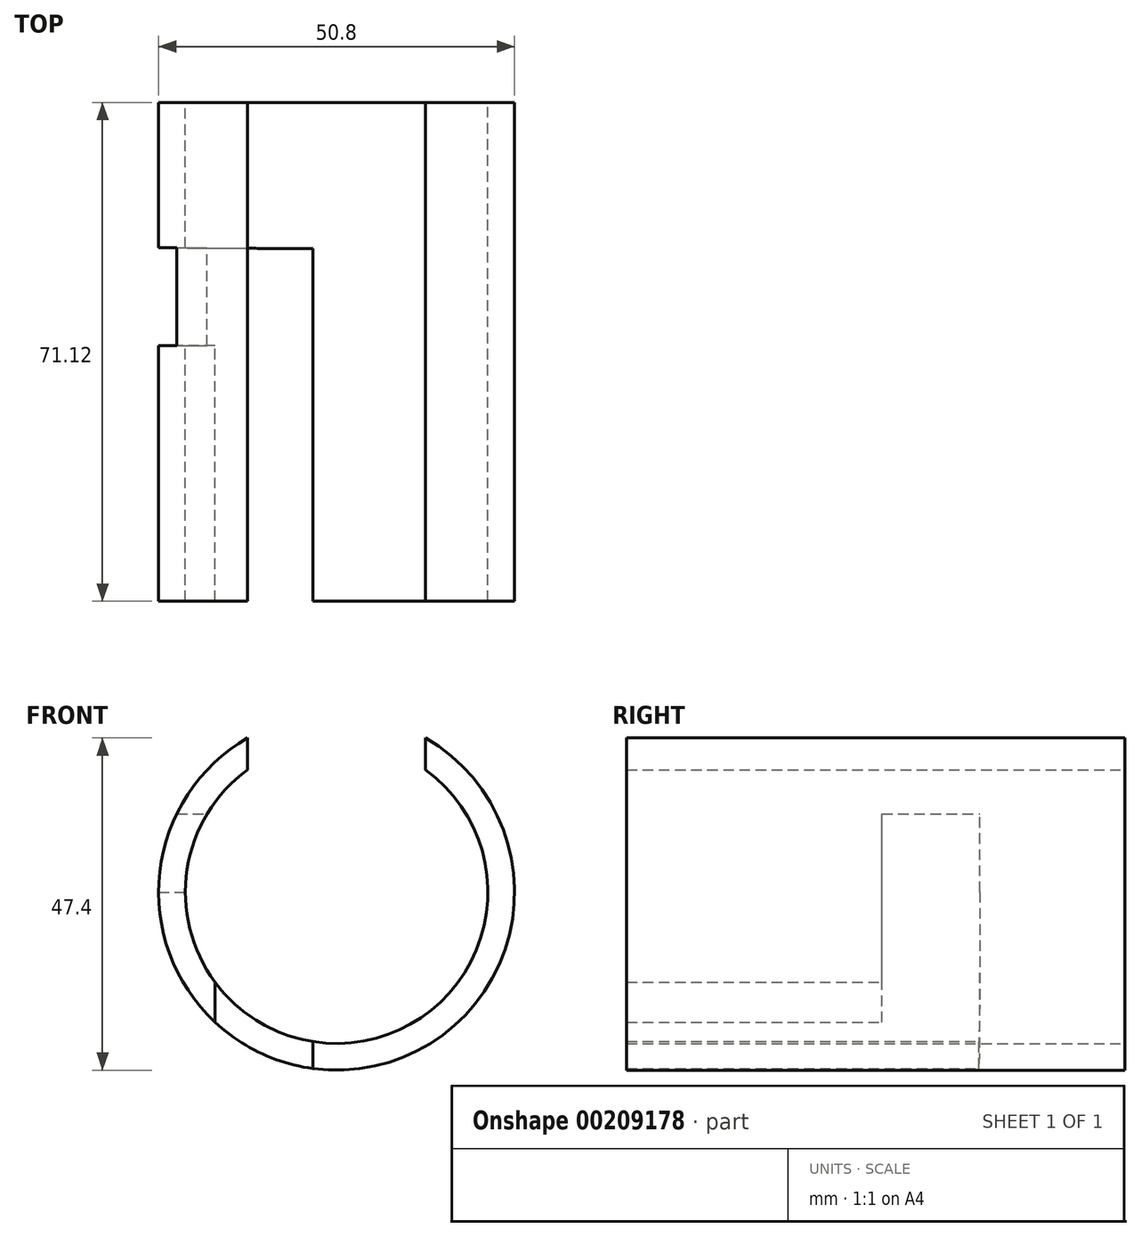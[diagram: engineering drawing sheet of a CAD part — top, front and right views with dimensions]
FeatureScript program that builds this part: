
annotation { "Feature Type Name" : "Feature", "Feature Type Description" : "" }
export const myFeature = defineFeature(function(context is Context, id is Id, definition is map)
    precondition{}
    {
        {
            var Q0;
            Q0=qCreatedBy(makeId("Front.planeOp"),FACE);
            var sketch = newSketch(context, id + "F0", { "sketchPlane" : qUnion([Q0])});
            skCircle(sketch, "E0", {"center": v(0, 0) * mm, "radius": 25.4 * mm});
            skCircle(sketch, "E1.0", {"center": v(0, 0) * mm, "radius": 21.59 * mm});
            skSolve(sketch);
        }
        {
            var Q0;
            Q0=makeQuery(id+"F0.imprint","IMPRINT",FACE,{"disambiguationData":[TD([[makeQuery(id+"F0.imprint","IMPRINT",EDGE,{"derivedFrom":sQuery(id+"F0.wireOp",EDGE,"E0")}),1.0]])]});
            extrude(context, id + "F1", {"entities" : qUnion([Q0]), "depth" : 71.12 * mm});
        }
        {
            var Q0;
            Q0=qCreatedBy(makeId("Top.planeOp"),FACE);
            var sketch = newSketch(context, id + "F2", { "sketchPlane" : qUnion([Q0])});
            skPoint(sketch, "E2", {"position": v(-17.35, -71.12) * mm});
            skPoint(sketch, "E3", {"position": v(-3.38, -71.12) * mm});
            skLineSegment(sketch, "E4", {"start": v(-17.35, -71.12) * mm, "end": v(-17.35, -34.67) * mm});
            skLineSegment(sketch, "E5", {"start": v(-3.38, -71.12) * mm, "end": v(-3.38, -34.67) * mm});
            skLineSegment(sketch, "E6", {"start": v(-3.38, -20.84) * mm, "end": v(-3.38, -34.67) * mm});
            skLineSegment(sketch, "E7", {"start": v(-17.35, -71.12) * mm, "end": v(-3.38, -71.12) * mm});
            skLineSegment(sketch, "E8", {"start": v(-17.35, -34.67) * mm, "end": v(-25.6, -34.67) * mm});
            skLineSegment(sketch, "E9", {"start": v(-25.6, -34.67) * mm, "end": v(-25.59, -20.7) * mm});
            skLineSegment(sketch, "E10", {"start": v(-25.59, -20.7) * mm, "end": v(-3.38, -20.84) * mm});
            skSolve(sketch);
        }
        {
            var Q0;
            Q0 = qSketchRegion(id + "F2", true);
            extrude(context, id + "F3", {"entities" : qUnion([Q0]), "operationType" : NewBodyOperationType.REMOVE, "oppositeDirection" : true, "depth" : 25.4 * mm});
        }
        {
            var Q0;
            Q0=qCreatedBy(makeId("Right.planeOp"),FACE);
            var sketch = newSketch(context, id + "F4", { "sketchPlane" : qUnion([Q0])});
            skPoint(sketch, "E11", {"position": v(-20.7, 0) * mm});
            skPoint(sketch, "E12", {"position": v(-34.67, 0) * mm});
            skLineSegment(sketch, "E13", {"start": v(-20.7, 0) * mm, "end": v(-20.7, 11.16) * mm});
            skLineSegment(sketch, "E14", {"start": v(-20.7, 11.16) * mm, "end": v(-34.67, 11.16) * mm});
            skLineSegment(sketch, "E15", {"start": v(-34.67, 11.16) * mm, "end": v(-34.67, 0) * mm});
            skLineSegment(sketch, "E16", {"start": v(-20.7, 0) * mm, "end": v(-34.67, 0) * mm});
            skSolve(sketch);
        }
        {
            var Q0;
            Q0 = qSketchRegion(id + "F4", true);
            extrude(context, id + "F5", {"entities" : qUnion([Q0]), "operationType" : NewBodyOperationType.REMOVE, "oppositeDirection" : true, "depth" : 25.4 * mm});
        }
        {
            var Q0;
            Q0=qCreatedBy(makeId("Top.planeOp"),FACE);
            var sketch = newSketch(context, id + "F6", { "sketchPlane" : qUnion([Q0])});
            skPoint(sketch, "E17", {"position": v(0, 0) * mm});
            skPoint(sketch, "E18", {"position": v(-12.7, 0) * mm});
            skPoint(sketch, "E19", {"position": v(12.7, 0) * mm});
            skLineSegment(sketch, "E20", {"start": v(-12.7, 0) * mm, "end": v(-12.7, -71.12) * mm});
            skLineSegment(sketch, "E21", {"start": v(12.7, -71.12) * mm, "end": v(12.7, 0) * mm});
            skLineSegment(sketch, "E22", {"start": v(-12.7, -71.12) * mm, "end": v(12.7, -71.12) * mm});
            skLineSegment(sketch, "E23", {"start": v(-12.7, 0) * mm, "end": v(12.7, 0) * mm});
            skSolve(sketch);
        }
        {
            var Q0;
            Q0=makeQuery(id+"F6.imprint","IMPRINT",FACE,{"disambiguationData":[TD([[makeQuery(id+"F6.imprint","IMPRINT",EDGE,{"derivedFrom":sQuery(id+"F6.wireOp",EDGE,"E20")}),1.0]])]});
            extrude(context, id + "F7", {"entities" : qUnion([Q0]), "operationType" : NewBodyOperationType.REMOVE, "depth" : 25.4 * mm});
        }
    });
